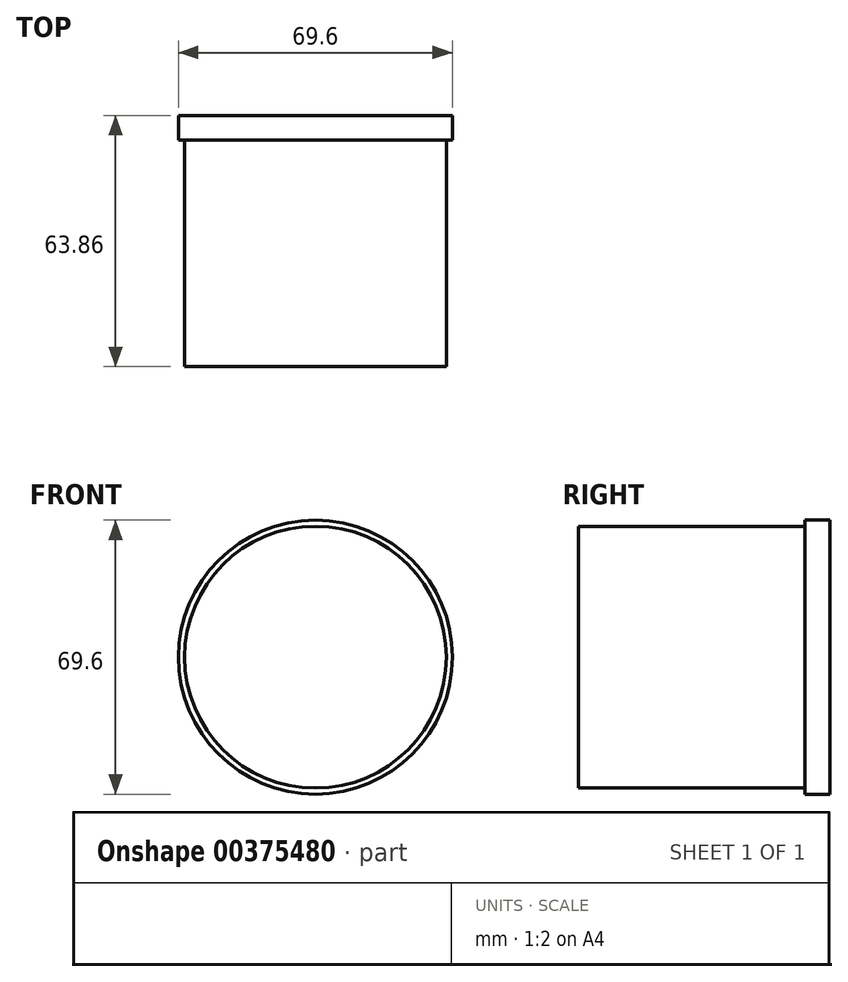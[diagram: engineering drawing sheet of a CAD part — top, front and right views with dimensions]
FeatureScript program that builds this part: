
annotation { "Feature Type Name" : "Feature", "Feature Type Description" : "" }
export const myFeature = defineFeature(function(context is Context, id is Id, definition is map)
    precondition{}
    {
        {
            var Q0;
            Q0=qCreatedBy(makeId("Front.planeOp"),FACE);
            var sketch = newSketch(context, id + "F0", { "sketchPlane" : qUnion([Q0])});
            skCircle(sketch, "E0", {"center": v(0, 0) * mm, "radius": 33.25 * mm});
            skSolve(sketch);
        }
        {
            var Q0;
            Q0=makeQuery(id+"F0.imprint","IMPRINT",FACE,{"disambiguationData":[TD([[makeQuery(id+"F0.imprint","IMPRINT",EDGE,{"derivedFrom":sQuery(id+"F0.wireOp",EDGE,"E0")}),1.0]])]});
            extrude(context, id + "F1", {"entities" : qUnion([Q0]), "depth" : 57.55 * mm});
        }
        {
            var Q0;
            Q0=qCreatedBy(makeId("Front.planeOp"),FACE);
            var sketch = newSketch(context, id + "F2", { "sketchPlane" : qUnion([Q0])});
            skCircle(sketch, "E1", {"center": v(0, 0) * mm, "radius": 34.8 * mm});
            skSolve(sketch);
        }
        {
            var Q0;
            Q0=makeQuery(id+"F2.imprint","IMPRINT",FACE,{"disambiguationData":[TD([[makeQuery(id+"F2.imprint","IMPRINT",EDGE,{"derivedFrom":sQuery(id+"F2.wireOp",EDGE,"E1")}),1.0]])]});
            extrude(context, id + "F3", {"entities" : qUnion([Q0]), "operationType" : NewBodyOperationType.ADD, "oppositeDirection" : true, "depth" : 6.3 * mm});
        }
    });
